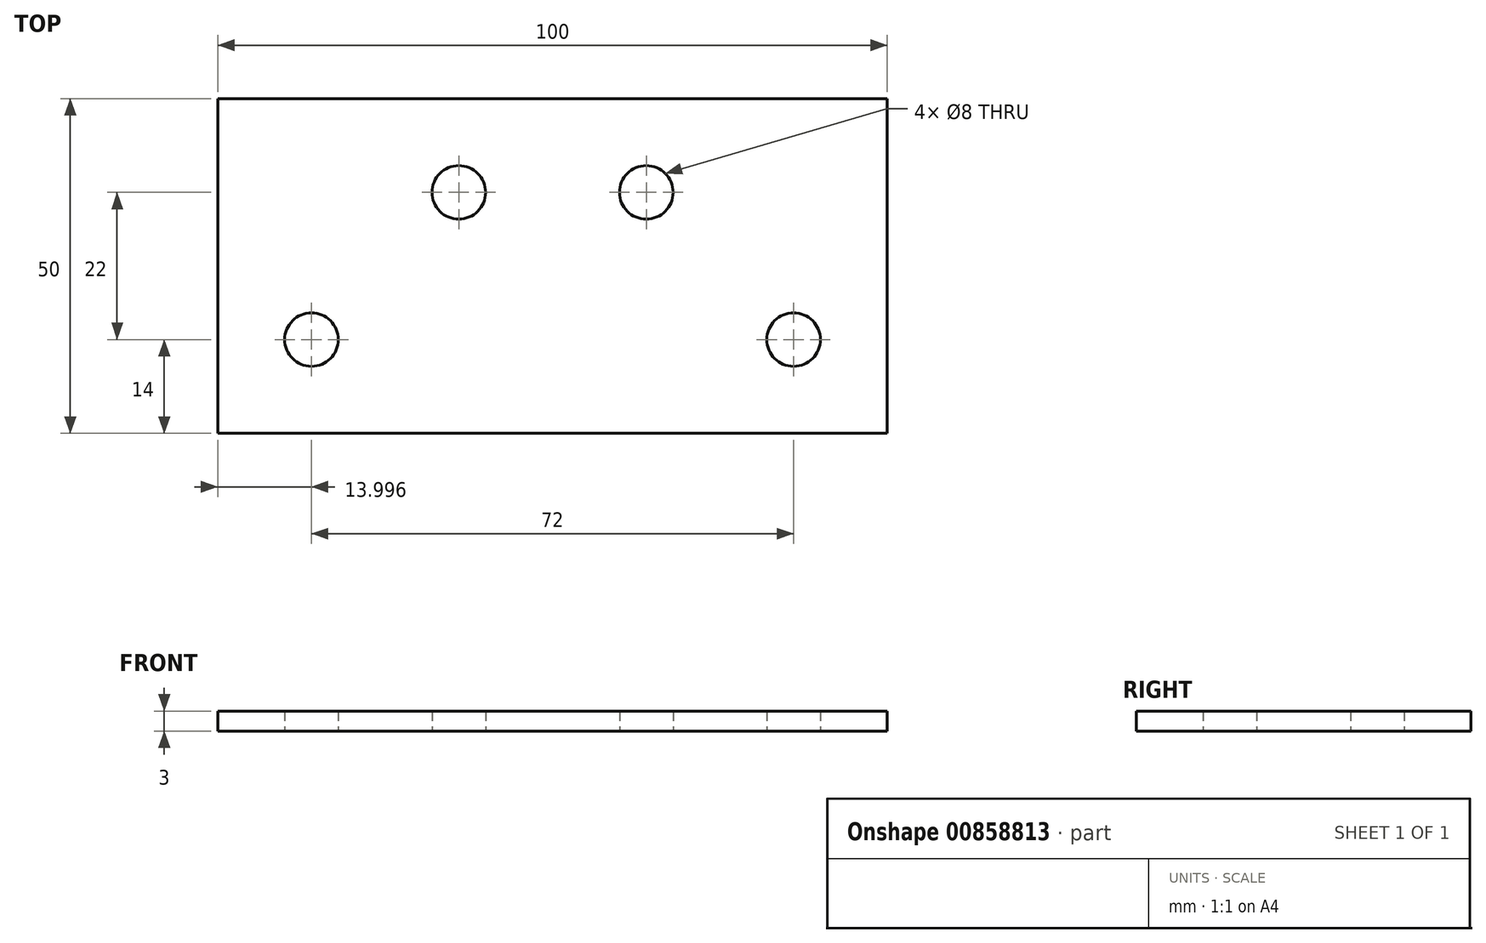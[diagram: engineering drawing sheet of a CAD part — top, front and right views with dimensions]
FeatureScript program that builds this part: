
annotation { "Feature Type Name" : "Feature", "Feature Type Description" : "" }
export const myFeature = defineFeature(function(context is Context, id is Id, definition is map)
    precondition{}
    {
        {
            var Q0;
            Q0=qCreatedBy(makeId("Top.planeOp"),FACE);
            var sketch = newSketch(context, id + "F0", { "sketchPlane" : qUnion([Q0])});
            skLineSegment(sketch, "E0.bottom", {"start": v(-45.3, 26.89) * mm, "end": v(54.7, 26.89) * mm});
            skLineSegment(sketch, "E0.top", {"start": v(-45.3, -23.11) * mm, "end": v(54.7, -23.11) * mm});
            skLineSegment(sketch, "E0.left", {"start": v(-45.3, 26.89) * mm, "end": v(-45.3, -23.11) * mm});
            skLineSegment(sketch, "E0.right", {"start": v(54.7, 26.89) * mm, "end": v(54.7, -23.11) * mm});
            skCircle(sketch, "E1", {"center": v(-31.3, -9.11) * mm, "radius": 4 * mm});
            skCircle(sketch, "E2", {"center": v(-9.3, 12.89) * mm, "radius": 4 * mm});
            skCircle(sketch, "E3", {"center": v(18.7, 12.89) * mm, "radius": 4 * mm});
            skCircle(sketch, "E4", {"center": v(40.7, -9.11) * mm, "radius": 4 * mm});
            skLineSegment(sketch, "E5", {"start": v(4.7, 29.75) * mm, "end": v(4.7, -41.52) * mm, "construction": true});
            skPoint(sketch, "E5.startSnap0", {"position": v(4.7, 26.89) * mm});
            skPoint(sketch, "E5.endSnap0", {"position": v(4.7, -23.11) * mm});
            skSolve(sketch);
        }
        {
            var Q0;
            Q0 = qSketchRegion(id + "F0", true);
            extrude(context, id + "F1", {"entities" : qUnion([Q0]), "depth" : 3 * mm, "offsetDistance" : 25 * mm});
        }
    });
